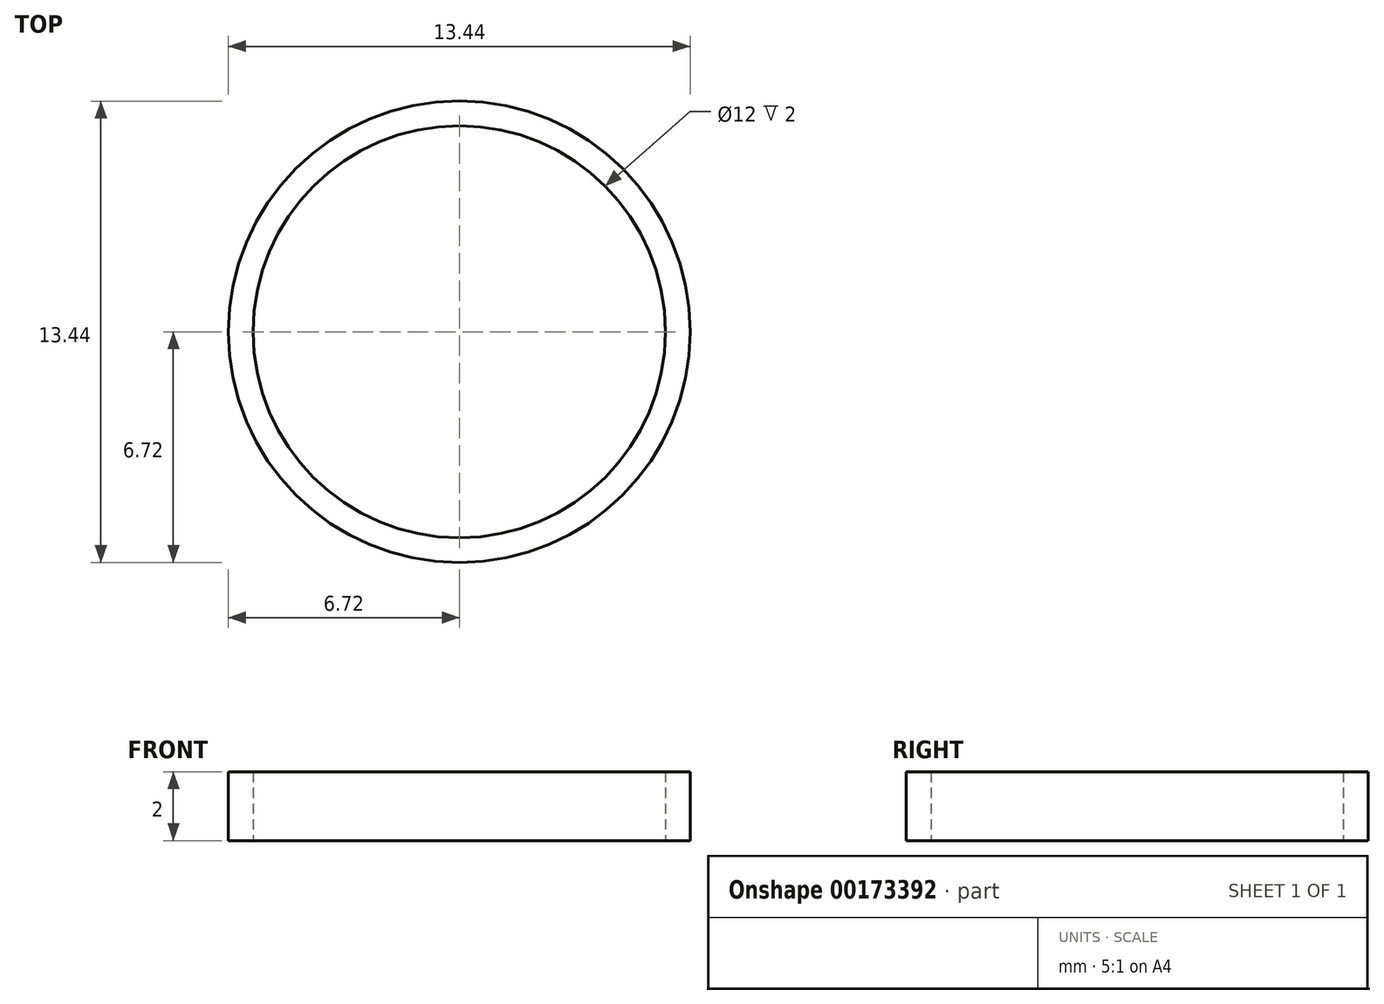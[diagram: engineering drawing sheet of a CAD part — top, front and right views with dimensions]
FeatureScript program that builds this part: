
annotation { "Feature Type Name" : "Feature", "Feature Type Description" : "" }
export const myFeature = defineFeature(function(context is Context, id is Id, definition is map)
    precondition{}
    {
        {
            var Q0;
            Q0=qCreatedBy(makeId("Top.planeOp"),FACE);
            var sketch = newSketch(context, id + "F0", { "sketchPlane" : qUnion([Q0])});
            skCircle(sketch, "E0", {"center": v(0, 0) * mm, "radius": 6.72 * mm});
            skCircle(sketch, "E1", {"center": v(0, 0) * mm, "radius": 6 * mm});
            skSolve(sketch);
        }
        {
            var Q0;
            Q0=makeQuery(id+"F0.imprint","IMPRINT",FACE,{"disambiguationData":[TD([[makeQuery(id+"F0.imprint","IMPRINT",EDGE,{"derivedFrom":sQuery(id+"F0.wireOp",EDGE,"E0")}),1.0]])]});
            var Q1;
            Q1=sQuery(id+"F0.wireOp",EDGE,"E1");
            var Q2;
            Q2=sQuery(id+"F0.wireOp",EDGE,"E0");
            extrude(context, id + "F1", {"entities" : qUnion([Q0]), "surfaceEntities" : qUnion([Q1, Q2]), "endBound" : BoundingType.SYMMETRIC, "depth" : 2 * mm});
        }
    });
